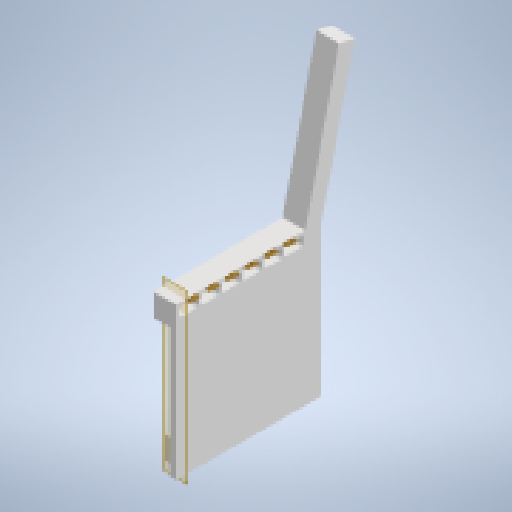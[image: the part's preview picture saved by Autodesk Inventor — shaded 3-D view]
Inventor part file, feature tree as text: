
AUTODESK INVENTOR PART (.ipt)
format: ipt  version: 2023 (Build 270158030, 158C)  size: 415,744 bytes
history: native  units: mm
features: extrude x7, sketch x7, reference x5, other x5, plane x1, pattern_linear x1, fillet x1, projected_geometry x1
ambient origin geometry x8: Origin, YZ Plane, XZ Plane, XY Plane, X Axis, Y Axis, Z Axis, Center Point
bodies: Solid1 (feature_tree)
feature tree (28):
  extrude  "Extrusion1"  Depth=70.0mm
  extrude  "Extrusion2"  Depth=70.0mm
  extrude  "Extrusion3"  Depth=400.0mm
  extrude  "Extrusion4"  [1 undecoded]
  plane  "Work Plane1"
  extrude  "Extrusion5"  Depth=450.0mm
  pattern_linear  "Rectangular Pattern1"  Count1=7 Spacing1=0.0mm
  extrude  "Extrusion6"  Depth=60.0mm
  fillet  "Fillet1"  Radius=30.0mm
  extrude  "Extrusion7"  Depth=10.0mm
  sketch  "Sketch1"  dims[d0=380.0mm d1=70.0mm]
  sketch  "Sketch2"  dims[d2=190.0mm d3=70.0mm]
  sketch  "Sketch3"  dims[d4=50.0mm d5=400.0mm]
  sketch  "Sketch4"  dims[d6=9.599311mm d7=-13.477291mm]
  projected_geometry  "Projected Loop1"
  sketch  "Sketch6"  dims[d8=70.0mm d9=450.0mm]
  reference  "Reference5"
  reference  "Reference6"
  reference  "Reference7"
  reference  "Reference8"
  reference  "Reference9"
  other  "hinges"
  sketch  "Sketch7"  dims[d10=35.0mm]
  other  "locating-pin"
  sketch  "Sketch8"  dims[d11=35.0mm d12=70.0mm d13=0.0mm d14=60.0mm d15=30.0mm d16=10.0mm d17=10.0mm d18=10.0mm d19=60.0mm d21=65.0mm d22=10.0mm d24=10.0mm d26=0.0mm d27=0.0mm d28=17.976891mm d29=50.0mm d30=50.0mm d31=450.0mm d32=450.0mm d33=10.0mm d34=0.0mm d35=20.0mm d36=0.0mm d37=-30.0mm d40=0.5mm d41=9.0mm d42=14.0mm d43=8.5mm d44=30.0mm d45=0.0mm d46=60.0mm d48=60.0mm d49=25.0mm d50=24.0mm d51=22.0mm d52=30.0mm d53=0.0mm d54=4.0mm d55=26.0mm d56=12.0mm d57=12.0mm d58=100.0mm d59=10.0mm d60=30.0mm d61=0.0mm]
  other  "<userpath>\Documents\0004-inventor\3D-CAD-main\primary-engineer-bench.iam"
  other  "primary-engineer-bench.iam"
  other  "flip-up-side:1"
note: 1 required parameter value undecoded (feature->parameter linkage not recoverable at this tier; creation-order binding heuristic only, values carry confidence <= 0.55)
